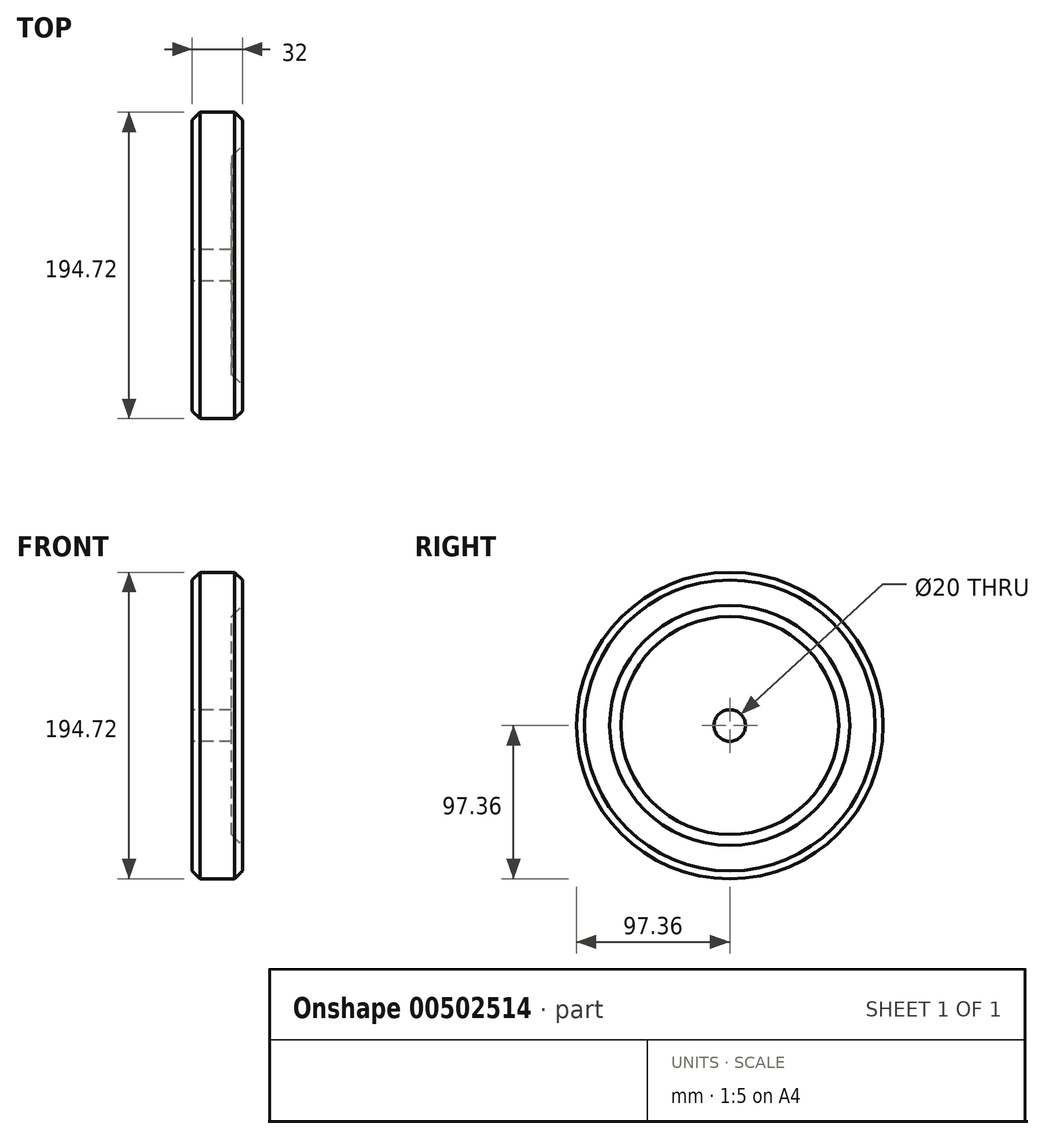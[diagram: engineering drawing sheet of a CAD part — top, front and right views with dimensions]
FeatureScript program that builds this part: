
annotation { "Feature Type Name" : "Feature", "Feature Type Description" : "" }
export const myFeature = defineFeature(function(context is Context, id is Id, definition is map)
    precondition{}
    {
        {
            var Q0;
            Q0=qCreatedBy(makeId("Right.planeOp"),FACE);
            var sketch = newSketch(context, id + "F0", { "sketchPlane" : qUnion([Q0])});
            skCircle(sketch, "E0", {"center": v(0, 0) * mm, "radius": 10 * mm});
            skCircle(sketch, "E1", {"center": v(0, 0) * mm, "radius": 66.22 * mm});
            skCircle(sketch, "E2", {"center": v(0, 0) * mm, "radius": 74.35 * mm});
            skCircle(sketch, "E3", {"center": v(0, 0) * mm, "radius": 97.36 * mm});
            skCircle(sketch, "E4", {"center": v(0, 0) * mm, "radius": 105.26 * mm});
            skSolve(sketch);
        }
        {
            var Q0;
            Q0=makeQuery(id+"F0.imprint","IMPRINT",FACE,{"disambiguationData":[TD([[makeQuery(id+"F0.imprint","IMPRINT",EDGE,{"derivedFrom":sQuery(id+"F0.wireOp",EDGE,"E0")}),-1.0]])]});
            extrude(context, id + "F1", {"entities" : qUnion([Q0]), "depth" : 25 * mm});
        }
        {
            var Q0;
            Q0=makeQuery(id+"F0.imprint","IMPRINT",FACE,{"disambiguationData":[TD([[makeQuery(id+"F0.imprint","IMPRINT",EDGE,{"derivedFrom":sQuery(id+"F0.wireOp",EDGE,"E1")}),-1.0]])]});
            var Q1;
            Q1=makeQuery(id+"F0.imprint","IMPRINT",FACE,{"disambiguationData":[TD([[makeQuery(id+"F0.imprint","IMPRINT",EDGE,{"derivedFrom":sQuery(id+"F0.wireOp",EDGE,"E2")}),-1.0]])]});
            extrude(context, id + "F2", {"entities" : qUnion([Q0, Q1]), "operationType" : NewBodyOperationType.ADD, "depth" : 32 * mm});
        }
        {
            var Q0;
            Q0=makeQuery(id+"F2.opExtrude","CAP_EDGE",EDGE,{"disambiguationData":[OSD([sQuery(id+"F0.wireOp",EDGE,"E1")])],"isStart":false});
            chamfer(context, id + "F3", {"entities" : qUnion([Q0]), "width" : 10 * mm, "tangentPropagation" : true});
        }
        {
            var Q0;
            Q0=makeQuery(id+"F2.opExtrude","CAP_EDGE",EDGE,{"disambiguationData":[OSD([sQuery(id+"F0.wireOp",EDGE,"E3")])],"isStart":false});
            chamfer(context, id + "F4", {"entities" : qUnion([Q0]), "width" : 5 * mm, "tangentPropagation" : true});
        }
        {
            var Q0;
            Q0=makeQuery(id+"F2.opExtrude","CAP_EDGE",EDGE,{"disambiguationData":[OSD([sQuery(id+"F0.wireOp",EDGE,"E3")])],"isStart":true});
            chamfer(context, id + "F5", {"entities" : qUnion([Q0]), "width" : 5 * mm, "tangentPropagation" : true});
        }
    });
